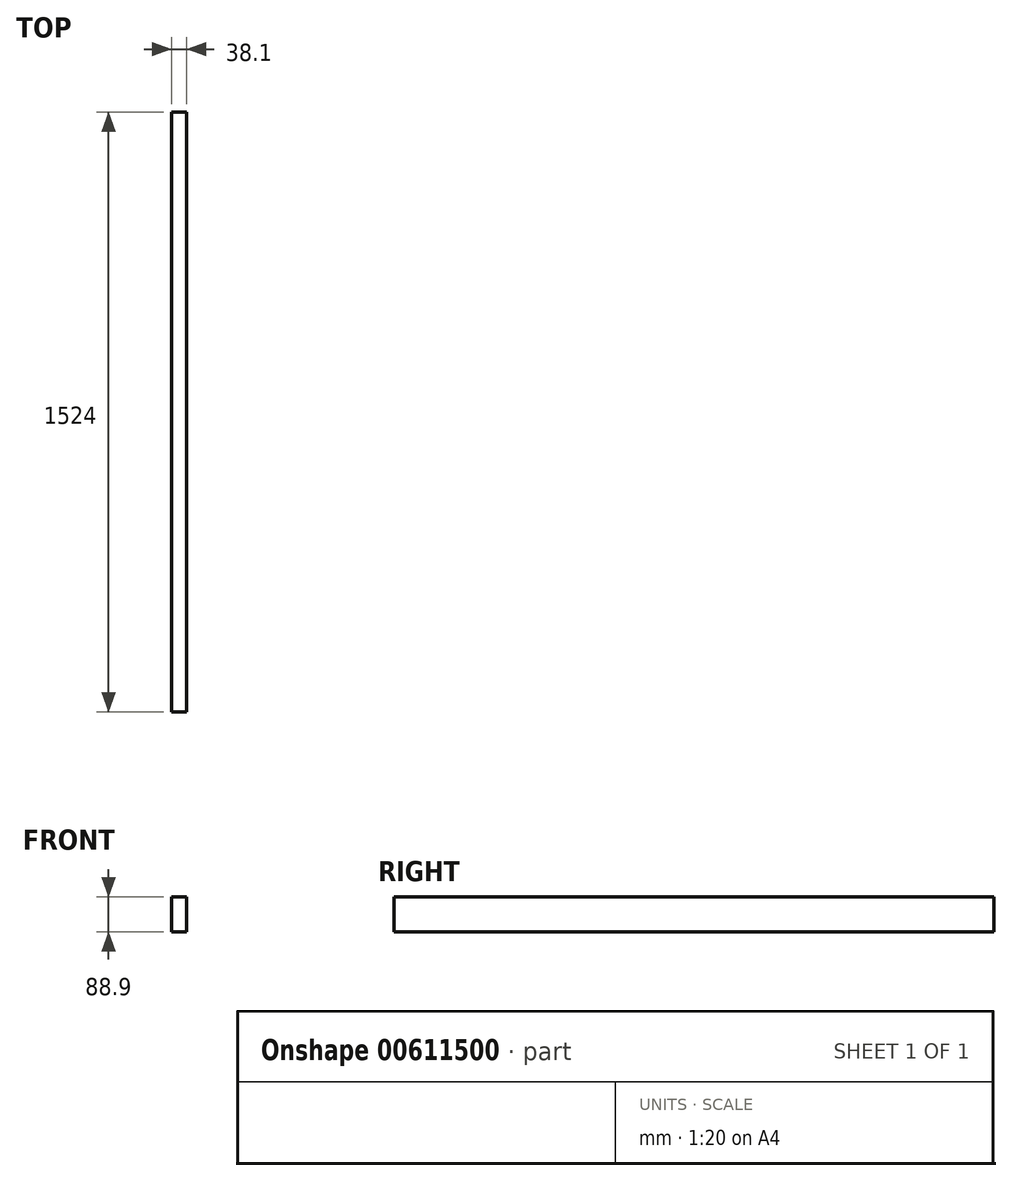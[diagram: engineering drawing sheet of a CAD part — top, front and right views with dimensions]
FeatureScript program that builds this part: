
annotation { "Feature Type Name" : "Feature", "Feature Type Description" : "" }
export const myFeature = defineFeature(function(context is Context, id is Id, definition is map)
    precondition{}
    {
        {
            var Q0;
            Q0=qCreatedBy(makeId("Front.planeOp"),FACE);
            var sketch = newSketch(context, id + "F0", { "sketchPlane" : qUnion([Q0])});
            skLineSegment(sketch, "E0.bottom", {"start": v(-21.25, 77.69) * mm, "end": v(16.85, 77.69) * mm});
            skLineSegment(sketch, "E0.top", {"start": v(-21.25, -11.21) * mm, "end": v(16.85, -11.21) * mm});
            skLineSegment(sketch, "E0.left", {"start": v(-21.25, 77.69) * mm, "end": v(-21.25, -11.21) * mm});
            skLineSegment(sketch, "E0.right", {"start": v(16.85, 77.69) * mm, "end": v(16.85, -11.21) * mm});
            skSolve(sketch);
        }
        {
            var Q0;
            Q0=makeQuery(id+"F0.imprint","IMPRINT",FACE,{"disambiguationData":[TD([[makeQuery(id+"F0.imprint","IMPRINT",EDGE,{"derivedFrom":sQuery(id+"F0.wireOp",EDGE,"E0.bottom")}),-1.0]])]});
            extrude(context, id + "F1", {"entities" : qUnion([Q0]), "depth" : 1524 * mm, "offsetDistance" : 25.4 * mm});
        }
    });
